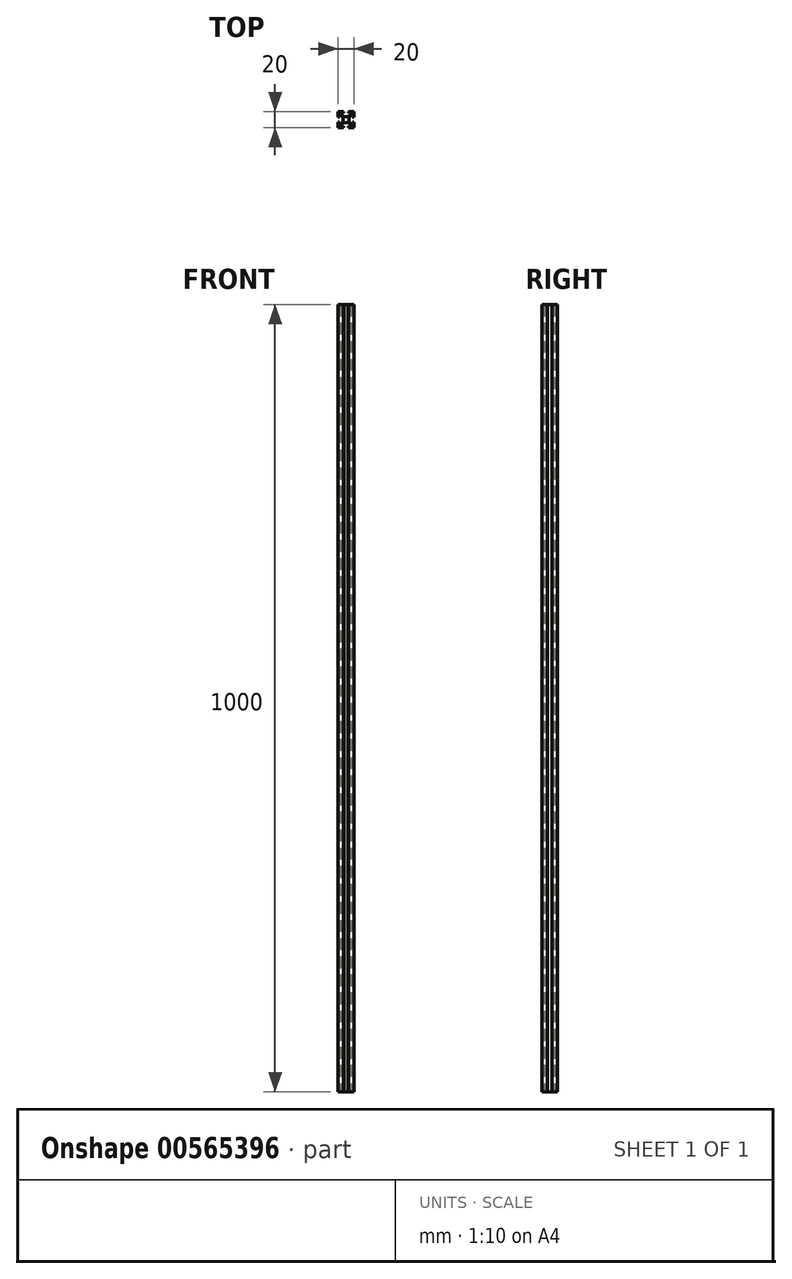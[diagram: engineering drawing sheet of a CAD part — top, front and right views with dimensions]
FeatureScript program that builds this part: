
annotation { "Feature Type Name" : "Feature", "Feature Type Description" : "" }
export const myFeature = defineFeature(function(context is Context, id is Id, definition is map)
    precondition{}
    {
        {
            var Q0;
            Q0=qCreatedBy(makeId("Top.planeOp"),FACE);
            var sketch = newSketch(context, id + "F0", { "sketchPlane" : qUnion([Q0])});
            skLineSegment(sketch, "E0", {"start": v(-10, 10) * mm, "end": v(-3, 10) * mm});
            skLineSegment(sketch, "E1", {"start": v(-3, 10) * mm, "end": v(-3, 8.2) * mm});
            skLineSegment(sketch, "E2", {"start": v(3, 8.2) * mm, "end": v(3, 10) * mm});
            skLineSegment(sketch, "E3", {"start": v(3, 10) * mm, "end": v(10, 10) * mm});
            skLineSegment(sketch, "E4", {"start": v(-10, 10) * mm, "end": v(-10, 3) * mm});
            skLineSegment(sketch, "E5", {"start": v(-10, 3) * mm, "end": v(-8.2, 3) * mm});
            skLineSegment(sketch, "E6", {"start": v(-10, -3) * mm, "end": v(-10, -10) * mm});
            skLineSegment(sketch, "E7", {"start": v(-10, -3) * mm, "end": v(-8.2, -3) * mm});
            skLineSegment(sketch, "E8", {"start": v(-10, -10) * mm, "end": v(-3, -10) * mm});
            skLineSegment(sketch, "E9", {"start": v(-3, -10) * mm, "end": v(-3, -8.2) * mm});
            skLineSegment(sketch, "E10", {"start": v(3, -10) * mm, "end": v(10, -10) * mm});
            skLineSegment(sketch, "E11", {"start": v(3, -10) * mm, "end": v(3, -8.2) * mm});
            skLineSegment(sketch, "E12", {"start": v(10, 10) * mm, "end": v(10, 3) * mm});
            skLineSegment(sketch, "E13", {"start": v(10, 3) * mm, "end": v(8.2, 3) * mm});
            skLineSegment(sketch, "E14", {"start": v(10, -10) * mm, "end": v(10, -3) * mm});
            skLineSegment(sketch, "E15", {"start": v(10, -3) * mm, "end": v(8.2, -3) * mm});
            skLineSegment(sketch, "E16", {"start": v(-3, -8.2) * mm, "end": v(-5.5, -8.2) * mm});
            skLineSegment(sketch, "E17", {"start": v(3, -8.2) * mm, "end": v(5.5, -8.2) * mm});
            skLineSegment(sketch, "E18", {"start": v(8.2, -3) * mm, "end": v(8.2, -5.5) * mm});
            skLineSegment(sketch, "E19", {"start": v(8.2, 3) * mm, "end": v(8.2, 5.5) * mm});
            skLineSegment(sketch, "E20", {"start": v(3, 8.2) * mm, "end": v(5.5, 8.2) * mm});
            skLineSegment(sketch, "E21", {"start": v(-3, 8.2) * mm, "end": v(-5.5, 8.2) * mm});
            skLineSegment(sketch, "E22", {"start": v(-8.2, 3) * mm, "end": v(-8.2, 5.5) * mm});
            skLineSegment(sketch, "E23", {"start": v(-8.2, -3) * mm, "end": v(-8.2, -5.5) * mm});
            skLineSegment(sketch, "E24", {"start": v(-8.2, -5.5) * mm, "end": v(-6.6, -5.5) * mm});
            skLineSegment(sketch, "E25", {"start": v(-8.2, 5.5) * mm, "end": v(-6.6, 5.5) * mm});
            skLineSegment(sketch, "E26", {"start": v(-5.5, -8.2) * mm, "end": v(-5.5, -6.6) * mm});
            skLineSegment(sketch, "E27", {"start": v(5.5, -8.2) * mm, "end": v(5.5, -6.6) * mm});
            skLineSegment(sketch, "E28", {"start": v(8.2, -5.5) * mm, "end": v(6.6, -5.5) * mm});
            skLineSegment(sketch, "E29", {"start": v(8.2, 5.5) * mm, "end": v(6.6, 5.5) * mm});
            skLineSegment(sketch, "E30", {"start": v(5.5, 8.2) * mm, "end": v(5.5, 6.6) * mm});
            skLineSegment(sketch, "E31", {"start": v(-5.5, 8.2) * mm, "end": v(-5.5, 6.6) * mm});
            skLineSegment(sketch, "E32", {"start": v(5.5, 6.6) * mm, "end": v(2.8, 3.9) * mm});
            skLineSegment(sketch, "E33", {"start": v(6.6, 5.5) * mm, "end": v(3.9, 2.8) * mm});
            skLineSegment(sketch, "E34", {"start": v(6.6, -5.5) * mm, "end": v(3.9, -2.8) * mm});
            skLineSegment(sketch, "E35", {"start": v(5.5, -6.6) * mm, "end": v(2.8, -3.9) * mm});
            skLineSegment(sketch, "E36", {"start": v(-5.5, -6.6) * mm, "end": v(-2.8, -3.9) * mm});
            skLineSegment(sketch, "E37", {"start": v(-6.6, -5.5) * mm, "end": v(-3.9, -2.8) * mm});
            skLineSegment(sketch, "E38", {"start": v(-6.6, 5.5) * mm, "end": v(-3.9, 2.8) * mm});
            skLineSegment(sketch, "E39", {"start": v(-5.5, 6.6) * mm, "end": v(-2.8, 3.9) * mm});
            skLineSegment(sketch, "E40", {"start": v(-2.8, 3.9) * mm, "end": v(2.8, 3.9) * mm});
            skLineSegment(sketch, "E41", {"start": v(3.9, 2.8) * mm, "end": v(3.9, -2.8) * mm});
            skLineSegment(sketch, "E42", {"start": v(2.8, -3.9) * mm, "end": v(-2.8, -3.9) * mm});
            skLineSegment(sketch, "E43", {"start": v(-3.9, -2.8) * mm, "end": v(-3.9, 2.8) * mm});
            skSolve(sketch);
        }
        {
            var Q0;
            Q0=makeQuery(id+"F0.imprint","IMPRINT",FACE,{"disambiguationData":[TD([[makeQuery(id+"F0.imprint","IMPRINT",EDGE,{"derivedFrom":sQuery(id+"F0.wireOp",EDGE,"E0")}),-1.0]])]});
            extrude(context, id + "F1", {"entities" : qUnion([Q0]), "depth" : 1000 * mm, "offsetDistance" : 25 * mm});
        }
    });
